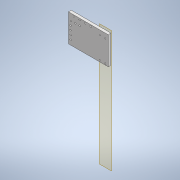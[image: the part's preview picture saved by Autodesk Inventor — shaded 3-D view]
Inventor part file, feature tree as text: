
AUTODESK INVENTOR PART (.ipt)
format: ipt  version: 2022 (Build 260153000, 153)  size: 164,352 bytes
history: native  units: in
note: dims shown in document units (in); Inventor stores cm internally (conversion verified against a paired STEP export)
features: reference x11, other x8, extrude x3, sketch x3, plane x1
ambient origin geometry x8: Origin, YZ Plane, XZ Plane, XY Plane, X Axis, Y Axis, Z Axis, Center Point
bodies: Solid1 (feature_tree)
feature tree (26):
  plane  "Work Plane1"
  extrude  "Extrusion1"  Depth=3.937in
  extrude  "Extrusion2"  Depth=0.1693in
  extrude  "Extrusion3"  Depth=0.3937in
  sketch  "Sketch1"  dims[d0=3.937in d1=0.1693in]
  reference  "Reference1"
  reference  "Reference2"
  reference  "Reference3"
  reference  "Reference4"
  reference  "Reference5"
  reference  "Reference6"
  reference  "Reference7"
  sketch  "Sketch2"  dims[d2=0.1693in d3=0.1693in]
  reference  "Reference8"
  reference  "Reference9"
  reference  "Reference10"
  sketch  "Sketch3"  dims[d4=0.1693in d5=0.1969in d6=0.1969in d7=0.1969in d8=0.1969in d9=0.2087in d10=0.7874in d11=1.5748in d13=0.7874in d14=0.3937in d16=0.3937in d18=0.3937in d19=0.0in d20=0.1969in d21=0.1969in d22=0.1969in d23=0.0in d24=0.0in d25=0.1969in d26=1.5748in d28=0.5906in d29=0.3937in d31=0.3937in d33=0.0in d34=0.0in]
  reference  "Reference11"
  other  "Linear Rail Assembly.iam"
  other  "endcap insert_MIR:1"
  other  "endcap insert:1"
  other  "Linear Rail End Cap:1"
  other  "Linear Rail Front Plate:1"
  other  "Linear Rail Base:1"
  other  "Linear Rail Frame Bracket_MIR:1"
  other  "Lower Support:1"
